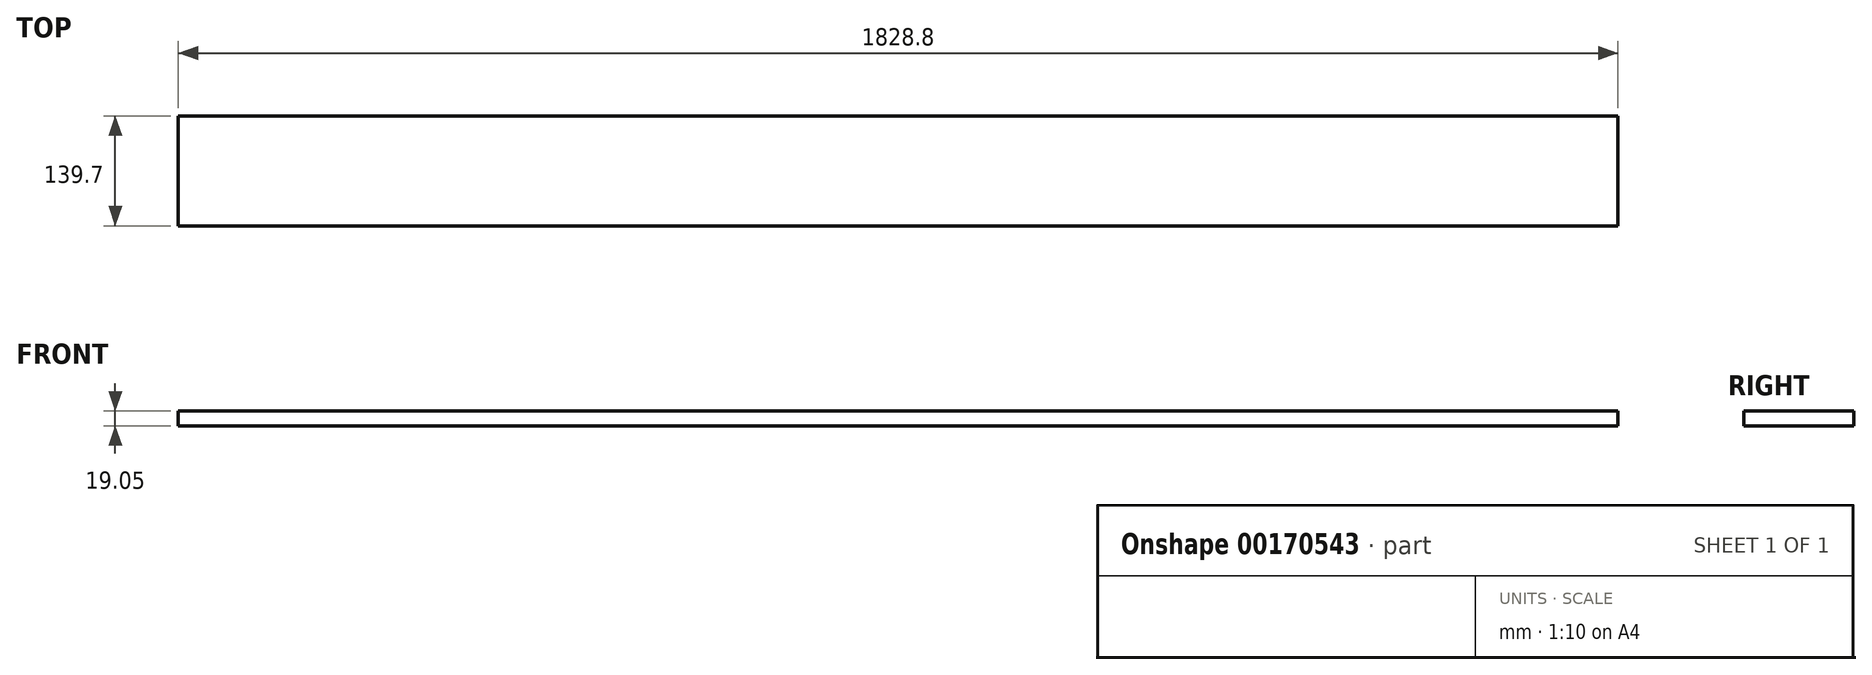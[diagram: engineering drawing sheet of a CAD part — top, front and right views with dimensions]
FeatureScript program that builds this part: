
annotation { "Feature Type Name" : "Feature", "Feature Type Description" : "" }
export const myFeature = defineFeature(function(context is Context, id is Id, definition is map)
    precondition{}
    {
        {
            var Q0;
            Q0=qCreatedBy(makeId("Top.planeOp"),FACE);
            var sketch = newSketch(context, id + "F0", { "sketchPlane" : qUnion([Q0])});
            skLineSegment(sketch, "E0.bottom", {"start": v(0, 0) * mm, "end": v(1828.8, 0) * mm});
            skLineSegment(sketch, "E0.top", {"start": v(0, 139.7) * mm, "end": v(1828.8, 139.7) * mm});
            skLineSegment(sketch, "E0.left", {"start": v(0, 0) * mm, "end": v(0, 139.7) * mm});
            skLineSegment(sketch, "E0.right", {"start": v(1828.8, 0) * mm, "end": v(1828.8, 139.7) * mm});
            skSolve(sketch);
        }
        {
            var Q0;
            Q0=makeQuery(id+"F0.imprint","IMPRINT",FACE,{"disambiguationData":[TD([[makeQuery(id+"F0.imprint","IMPRINT",EDGE,{"derivedFrom":sQuery(id+"F0.wireOp",EDGE,"E0.bottom")}),1.0]])]});
            extrude(context, id + "F1", {"entities" : qUnion([Q0]), "depth" : 19.05 * mm});
        }
    });
